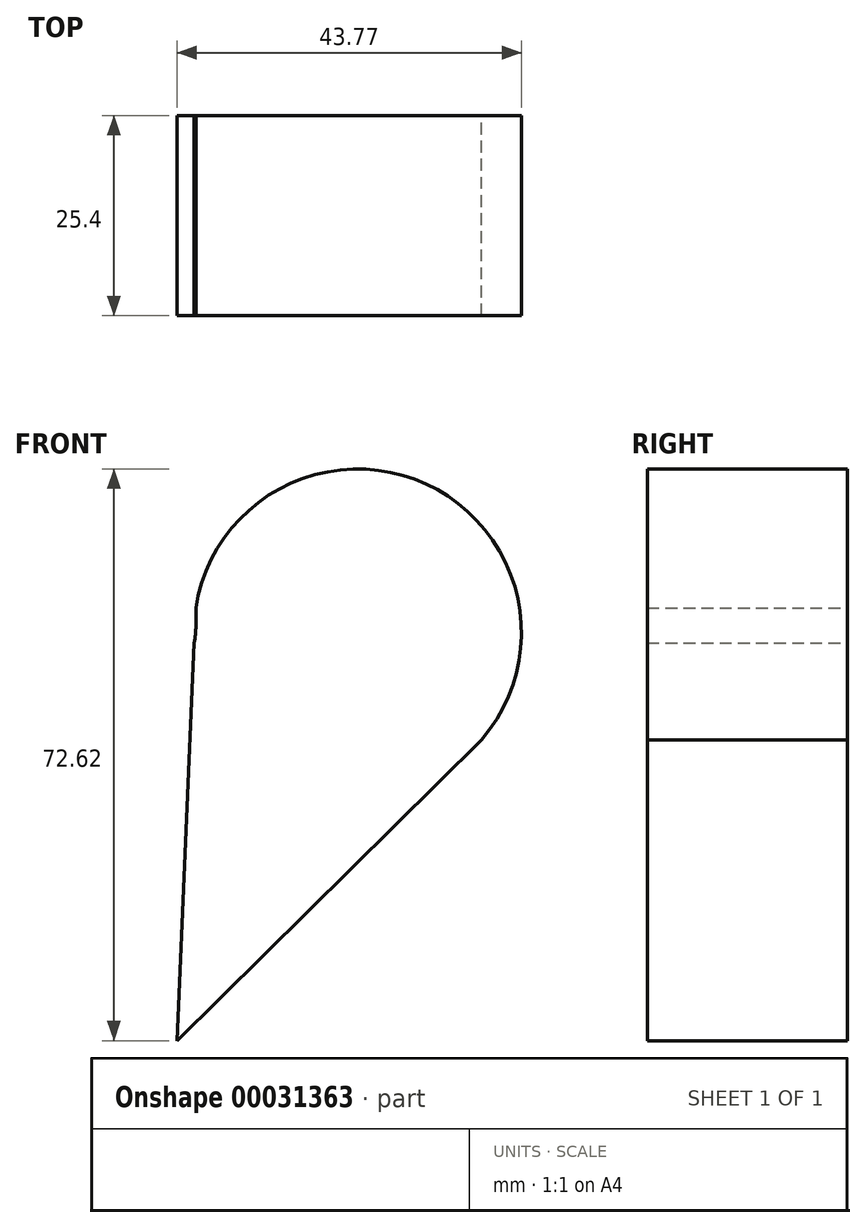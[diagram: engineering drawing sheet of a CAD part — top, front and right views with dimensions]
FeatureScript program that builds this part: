
annotation { "Feature Type Name" : "Feature", "Feature Type Description" : "" }
export const myFeature = defineFeature(function(context is Context, id is Id, definition is map)
    precondition{}
    {
        {
            var Q0;
            Q0=qCreatedBy(makeId("Front.planeOp"),FACE);
            var sketch = newSketch(context, id + "F0", { "sketchPlane" : qUnion([Q0])});
            skCircle(sketch, "E0", {"center": v(22.97, 21.54) * mm, "radius": 20.8 * mm});
            skLineSegment(sketch, "E1", {"start": v(2.21, 20.23) * mm, "end": v(0, -30.28) * mm});
            skLineSegment(sketch, "E2", {"start": v(0, -30.28) * mm, "end": v(38.7, 7.94) * mm});
            skCircle(sketch, "E3.MirrorC", {"center": v(-18.35, 23.35) * mm, "radius": 20.8 * mm});
            skSolve(sketch);
        }
        {
            var Q0;
            {var subQ3=sQuery(id+"F0.wireOp",EDGE,"E1");Q0=makeQuery(id+"F0.imprint","IMPRINT",FACE,{"disambiguationData":[TD([[makeQuery(id+"F0.imprint","IMPRINT",EDGE,{"derivedFrom":subQ3}),1.0]])]});}
            var Q1;
            {var subQ1=sQuery(id+"F0.wireOp",EDGE,"E0");var subQ4=sQuery(id+"F0.wireOp",EDGE,"E2");var subQ6=makeQuery(id+"F0.imprint","INTERSECT",VERTEX,{"disambiguationData":[OD(0.0)],"derivedFrom":[subQ1,subQ4]});Q1=makeQuery(id+"F0.imprint","IMPRINT",FACE,{"disambiguationData":[TD([[makeQuery(id+"F0.imprint","IMPRINT",EDGE,{"disambiguationData":[TD([[subQ6,-1.0]])],"derivedFrom":subQ1}),1.0]])]});}
            var Q2;
            {var subQ0=sQuery(id+"F0.wireOp",EDGE,"E3.MirrorC");var subQ1=sQuery(id+"F0.wireOp",EDGE,"E0");var subQ2=makeQuery(id+"F0.imprint","INTERSECT",VERTEX,{"derivedFrom":[subQ1,subQ0]});Q2=makeQuery(id+"F0.imprint","IMPRINT",FACE,{"disambiguationData":[TD([[makeQuery(id+"F0.imprint","IMPRINT",EDGE,{"disambiguationData":[TD([[subQ2,-1.0]])],"derivedFrom":subQ1}),-1.0]])]});}
            extrude(context, id + "F1", {"entities" : qUnion([Q0, Q1, Q2]), "depth" : 25.4 * mm});
        }
        {
            var Q0;
            Q0=makeQuery(id+"F1.opExtrude","SWEPT_BODY",BODY,{"disambiguationData":[OSD([sQuery(id+"F0.wireOp",EDGE,"E0"),sQuery(id+"F0.wireOp",EDGE,"E3.MirrorC")])]});
            deleteBodies(context, id + "F2", {"entities" : qUnion([Q0])});
        }
    });
